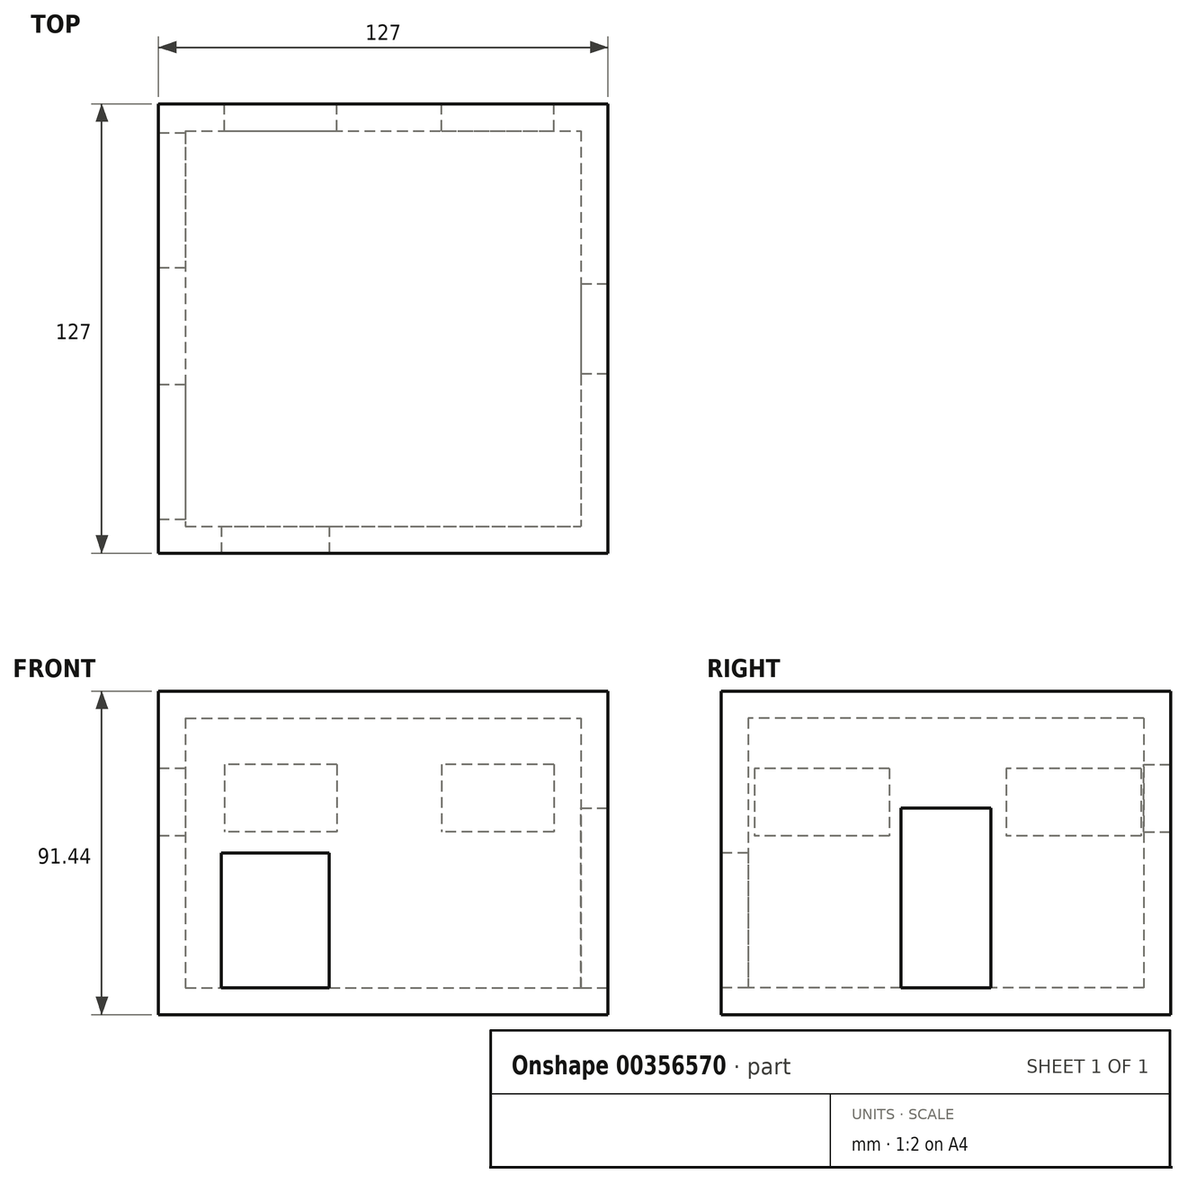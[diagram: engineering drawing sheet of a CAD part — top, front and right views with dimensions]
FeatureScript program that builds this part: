
annotation { "Feature Type Name" : "Feature", "Feature Type Description" : "" }
export const myFeature = defineFeature(function(context is Context, id is Id, definition is map)
    precondition{}
    {
        {
            var Q0;
            Q0=qCreatedBy(makeId("Top.planeOp"),FACE);
            var sketch = newSketch(context, id + "F0", { "sketchPlane" : qUnion([Q0])});
            skLineSegment(sketch, "E0.bottom", {"start": v(63.5, -63.5) * mm, "end": v(-63.5, -63.5) * mm});
            skLineSegment(sketch, "E0.top", {"start": v(63.5, 63.5) * mm, "end": v(-63.5, 63.5) * mm});
            skLineSegment(sketch, "E0.left", {"start": v(63.5, -63.5) * mm, "end": v(63.5, 63.5) * mm});
            skLineSegment(sketch, "E0.right", {"start": v(-63.5, -63.5) * mm, "end": v(-63.5, 63.5) * mm});
            skPoint(sketch, "E0.middle", {"position": v(0, 0) * mm});
            skSolve(sketch);
        }
        {
            var Q0;
            Q0 = qSketchRegion(id + "F0", true);
            extrude(context, id + "F1", {"entities" : qUnion([Q0]), "depth" : 7.62 * mm});
        }
        {
            var Q0;
            Q0=makeQuery(id+"F1.opExtrude","CAP_FACE",FACE,{"disambiguationData":[OSD([sQuery(id+"F0.wireOp",EDGE,"E0.bottom"),sQuery(id+"F0.wireOp",EDGE,"E0.top"),sQuery(id+"F0.wireOp",EDGE,"E0.left"),sQuery(id+"F0.wireOp",EDGE,"E0.right")])],"isStart":false});
            var sketch = newSketch(context, id + "F2", { "sketchPlane" : qUnion([Q0])});
            skLineSegment(sketch, "E1.bottom", {"start": v(-63.5, 63.5) * mm, "end": v(-55.88, 63.5) * mm});
            skLineSegment(sketch, "E1.top", {"start": v(-63.5, -63.5) * mm, "end": v(-55.88, -63.5) * mm});
            skLineSegment(sketch, "E1.left", {"start": v(-63.5, 63.5) * mm, "end": v(-63.5, -63.5) * mm});
            skLineSegment(sketch, "E1.right", {"start": v(-55.88, 63.5) * mm, "end": v(-55.88, -63.5) * mm});
            skLineSegment(sketch, "E2.bottom", {"start": v(63.5, 63.5) * mm, "end": v(55.88, 63.5) * mm});
            skLineSegment(sketch, "E2.top", {"start": v(63.5, -63.5) * mm, "end": v(55.88, -63.5) * mm});
            skLineSegment(sketch, "E2.left", {"start": v(63.5, 63.5) * mm, "end": v(63.5, -63.5) * mm});
            skLineSegment(sketch, "E2.right", {"start": v(55.88, 63.5) * mm, "end": v(55.88, -63.5) * mm});
            skLineSegment(sketch, "E3.bottom", {"start": v(-55.88, 63.5) * mm, "end": v(55.88, 63.5) * mm});
            skLineSegment(sketch, "E3.top", {"start": v(-55.88, 55.88) * mm, "end": v(55.88, 55.88) * mm});
            skLineSegment(sketch, "E3.left", {"start": v(-55.88, 63.5) * mm, "end": v(-55.88, 55.88) * mm});
            skLineSegment(sketch, "E3.right", {"start": v(55.88, 63.5) * mm, "end": v(55.88, 55.88) * mm});
            skLineSegment(sketch, "E4.bottom", {"start": v(-55.88, -55.88) * mm, "end": v(55.88, -55.88) * mm});
            skLineSegment(sketch, "E4.top", {"start": v(-55.88, -63.5) * mm, "end": v(55.88, -63.5) * mm});
            skLineSegment(sketch, "E4.left", {"start": v(-55.88, -55.88) * mm, "end": v(-55.88, -63.5) * mm});
            skLineSegment(sketch, "E4.right", {"start": v(55.88, -55.88) * mm, "end": v(55.88, -63.5) * mm});
            skSolve(sketch);
        }
        {
            var Q0;
            Q0 = qSketchRegion(id + "F2", true);
            extrude(context, id + "F3", {"entities" : qUnion([Q0]), "operationType" : NewBodyOperationType.ADD, "depth" : 76.2 * mm});
        }
        {
            var Q0;
            Q0=makeQuery(id+"F3.boolean.opBoolean","MERGE",FACE,{"derivedFrom":[makeQuery(id+"F1.opExtrude","SWEPT_FACE",FACE,{"disambiguationData":[OSD([sQuery(id+"F0.wireOp",EDGE,"E0.left")])]}),makeQuery(id+"F3.opExtrude","SWEPT_FACE",FACE,{"disambiguationData":[OSD([sQuery(id+"F2.wireOp",EDGE,"E2.left")])]})]});
            var sketch = newSketch(context, id + "F4", { "sketchPlane" : qUnion([Q0])});
            skLineSegment(sketch, "E5.bottom", {"start": v(-12.7, 58.42) * mm, "end": v(12.7, 58.42) * mm});
            skLineSegment(sketch, "E5.top", {"start": v(-12.7, 7.62) * mm, "end": v(12.7, 7.62) * mm});
            skLineSegment(sketch, "E5.left", {"start": v(-12.7, 58.42) * mm, "end": v(-12.7, 7.62) * mm});
            skLineSegment(sketch, "E5.right", {"start": v(12.7, 58.42) * mm, "end": v(12.7, 7.62) * mm});
            skLineSegment(sketch, "E6.bottom", {"start": v(-58.42, 76.2) * mm, "end": v(-26.67, 76.2) * mm});
            skLineSegment(sketch, "E6.top", {"start": v(-58.42, 50.8) * mm, "end": v(-26.67, 50.8) * mm});
            skLineSegment(sketch, "E6.left", {"start": v(-58.42, 76.2) * mm, "end": v(-58.42, 50.8) * mm});
            skLineSegment(sketch, "E6.right", {"start": v(-26.67, 76.2) * mm, "end": v(-26.67, 50.8) * mm});
            skLineSegment(sketch, "E7.bottom", {"start": v(26.67, 76.2) * mm, "end": v(58.42, 76.2) * mm});
            skLineSegment(sketch, "E7.top", {"start": v(26.67, 50.8) * mm, "end": v(58.42, 50.8) * mm});
            skLineSegment(sketch, "E7.left", {"start": v(26.67, 76.2) * mm, "end": v(26.67, 50.8) * mm});
            skLineSegment(sketch, "E7.right", {"start": v(58.42, 76.2) * mm, "end": v(58.42, 50.8) * mm});
            skSolve(sketch);
        }
        {
            var Q0;
            Q0=makeQuery(id+"F4.imprint","IMPRINT",FACE,{"disambiguationData":[TD([[makeQuery(id+"F4.imprint","IMPRINT",EDGE,{"derivedFrom":sQuery(id+"F4.wireOp",EDGE,"E5.bottom")}),-1.0]])]});
            extrude(context, id + "F5", {"entities" : qUnion([Q0]), "operationType" : NewBodyOperationType.REMOVE, "endBound" : BoundingType.UP_TO_NEXT, "oppositeDirection" : true, "depth" : 25.4 * mm});
        }
        {
            var Q0;
            Q0=makeQuery(id+"F3.boolean.opBoolean","MERGE",FACE,{"derivedFrom":[makeQuery(id+"F1.opExtrude","SWEPT_FACE",FACE,{"disambiguationData":[OSD([sQuery(id+"F0.wireOp",EDGE,"E0.top")])]}),makeQuery(id+"F3.opExtrude","SWEPT_FACE",FACE,{"disambiguationData":[OSD([sQuery(id+"F2.wireOp",EDGE,"E1.bottom"),sQuery(id+"F2.wireOp",EDGE,"E2.bottom"),sQuery(id+"F2.wireOp",EDGE,"E3.bottom")])]})]});
            var sketch = newSketch(context, id + "F6", { "sketchPlane" : qUnion([Q0])});
            skLineSegment(sketch, "E8.bottom", {"start": v(-48.17, 70.68) * mm, "end": v(-16.42, 70.68) * mm});
            skLineSegment(sketch, "E8.top", {"start": v(-48.17, 51.63) * mm, "end": v(-16.42, 51.63) * mm});
            skLineSegment(sketch, "E8.left", {"start": v(-48.17, 70.68) * mm, "end": v(-48.17, 51.63) * mm});
            skLineSegment(sketch, "E8.right", {"start": v(-16.42, 70.68) * mm, "end": v(-16.42, 51.63) * mm});
            skLineSegment(sketch, "E9.bottom", {"start": v(13.06, 70.68) * mm, "end": v(44.81, 70.68) * mm});
            skLineSegment(sketch, "E9.top", {"start": v(13.06, 51.63) * mm, "end": v(44.81, 51.63) * mm});
            skLineSegment(sketch, "E9.left", {"start": v(13.06, 70.68) * mm, "end": v(13.06, 51.63) * mm});
            skLineSegment(sketch, "E9.right", {"start": v(44.81, 70.68) * mm, "end": v(44.81, 51.63) * mm});
            skSolve(sketch);
        }
        {
            var Q0;
            Q0 = qSketchRegion(id + "F6", true);
            extrude(context, id + "F7", {"entities" : qUnion([Q0]), "operationType" : NewBodyOperationType.REMOVE, "endBound" : BoundingType.UP_TO_NEXT, "oppositeDirection" : true, "depth" : 25.4 * mm});
        }
        {
            var Q0;
            Q0=makeQuery(id+"F3.boolean.opBoolean","MERGE",FACE,{"derivedFrom":[makeQuery(id+"F1.opExtrude","SWEPT_FACE",FACE,{"disambiguationData":[OSD([sQuery(id+"F0.wireOp",EDGE,"E0.right")])]}),makeQuery(id+"F3.opExtrude","SWEPT_FACE",FACE,{"disambiguationData":[OSD([sQuery(id+"F2.wireOp",EDGE,"E1.left")])]})]});
            var sketch = newSketch(context, id + "F8", { "sketchPlane" : qUnion([Q0])});
            skLineSegment(sketch, "E10.bottom", {"start": v(-55.15, 69.58) * mm, "end": v(-17.05, 69.58) * mm});
            skLineSegment(sketch, "E10.top", {"start": v(-55.15, 50.53) * mm, "end": v(-17.05, 50.53) * mm});
            skLineSegment(sketch, "E10.left", {"start": v(-55.15, 69.58) * mm, "end": v(-55.15, 50.53) * mm});
            skLineSegment(sketch, "E10.right", {"start": v(-17.05, 69.58) * mm, "end": v(-17.05, 50.53) * mm});
            skLineSegment(sketch, "E11.bottom", {"start": v(16, 69.58) * mm, "end": v(54.1, 69.58) * mm});
            skLineSegment(sketch, "E11.top", {"start": v(16, 50.53) * mm, "end": v(54.1, 50.53) * mm});
            skLineSegment(sketch, "E11.left", {"start": v(16, 69.58) * mm, "end": v(16, 50.53) * mm});
            skLineSegment(sketch, "E11.right", {"start": v(54.1, 69.58) * mm, "end": v(54.1, 50.53) * mm});
            skSolve(sketch);
        }
        {
            var Q0;
            Q0 = qSketchRegion(id + "F8", true);
            extrude(context, id + "F9", {"entities" : qUnion([Q0]), "operationType" : NewBodyOperationType.REMOVE, "endBound" : BoundingType.UP_TO_NEXT, "oppositeDirection" : true, "depth" : 25.4 * mm});
        }
        {
            var Q0;
            Q0=makeQuery(id+"F3.opExtrude","CAP_FACE",FACE,{"disambiguationData":[OSD([sQuery(id+"F2.wireOp",EDGE,"E1.bottom"),sQuery(id+"F2.wireOp",EDGE,"E1.top"),sQuery(id+"F2.wireOp",EDGE,"E1.left"),sQuery(id+"F2.wireOp",EDGE,"E1.right"),sQuery(id+"F2.wireOp",EDGE,"E2.bottom"),sQuery(id+"F2.wireOp",EDGE,"E2.top"),sQuery(id+"F2.wireOp",EDGE,"E2.left"),sQuery(id+"F2.wireOp",EDGE,"E2.right"),sQuery(id+"F2.wireOp",EDGE,"E3.bottom"),sQuery(id+"F2.wireOp",EDGE,"E3.top"),sQuery(id+"F2.wireOp",EDGE,"E4.bottom"),sQuery(id+"F2.wireOp",EDGE,"E4.top")])],"isStart":false});
            var sketch = newSketch(context, id + "F10", { "sketchPlane" : qUnion([Q0])});
            skLineSegment(sketch, "E12.bottom", {"start": v(-63.5, 63.5) * mm, "end": v(63.5, 63.5) * mm});
            skLineSegment(sketch, "E12.top", {"start": v(-63.5, -63.5) * mm, "end": v(63.5, -63.5) * mm});
            skLineSegment(sketch, "E12.left", {"start": v(-63.5, 63.5) * mm, "end": v(-63.5, -63.5) * mm});
            skLineSegment(sketch, "E12.right", {"start": v(63.5, 63.5) * mm, "end": v(63.5, -63.5) * mm});
            skSolve(sketch);
        }
        {
            var Q0;
            Q0 = qSketchRegion(id + "F10", true);
            extrude(context, id + "F11", {"entities" : qUnion([Q0]), "operationType" : NewBodyOperationType.ADD, "depth" : 7.62 * mm});
        }
        {
            var Q0;
            Q0=makeQuery(id+"F11.boolean.opBoolean","MERGE",FACE,{"derivedFrom":[makeQuery(id+"F3.boolean.opBoolean","MERGE",FACE,{"derivedFrom":[makeQuery(id+"F1.opExtrude","SWEPT_FACE",FACE,{"disambiguationData":[OSD([sQuery(id+"F0.wireOp",EDGE,"E0.bottom")])]}),makeQuery(id+"F3.opExtrude","SWEPT_FACE",FACE,{"disambiguationData":[OSD([sQuery(id+"F2.wireOp",EDGE,"E1.top"),sQuery(id+"F2.wireOp",EDGE,"E2.top"),sQuery(id+"F2.wireOp",EDGE,"E4.top")])]})]}),makeQuery(id+"F11.opExtrude","SWEPT_FACE",FACE,{"disambiguationData":[OSD([sQuery(id+"F10.wireOp",EDGE,"E12.top")])]})]});
            var sketch = newSketch(context, id + "F12", { "sketchPlane" : qUnion([Q0])});
            skLineSegment(sketch, "E13.bottom", {"start": v(-45.74, 45.72) * mm, "end": v(-15.26, 45.72) * mm});
            skLineSegment(sketch, "E13.top", {"start": v(-45.74, 7.62) * mm, "end": v(-15.26, 7.62) * mm});
            skLineSegment(sketch, "E13.left", {"start": v(-45.74, 45.72) * mm, "end": v(-45.74, 7.62) * mm});
            skLineSegment(sketch, "E13.right", {"start": v(-15.26, 45.72) * mm, "end": v(-15.26, 7.62) * mm});
            skSolve(sketch);
        }
        {
            var Q0;
            Q0 = qSketchRegion(id + "F12", true);
            extrude(context, id + "F13", {"entities" : qUnion([Q0]), "operationType" : NewBodyOperationType.REMOVE, "endBound" : BoundingType.UP_TO_NEXT, "oppositeDirection" : true, "depth" : 25.4 * mm});
        }
    });
